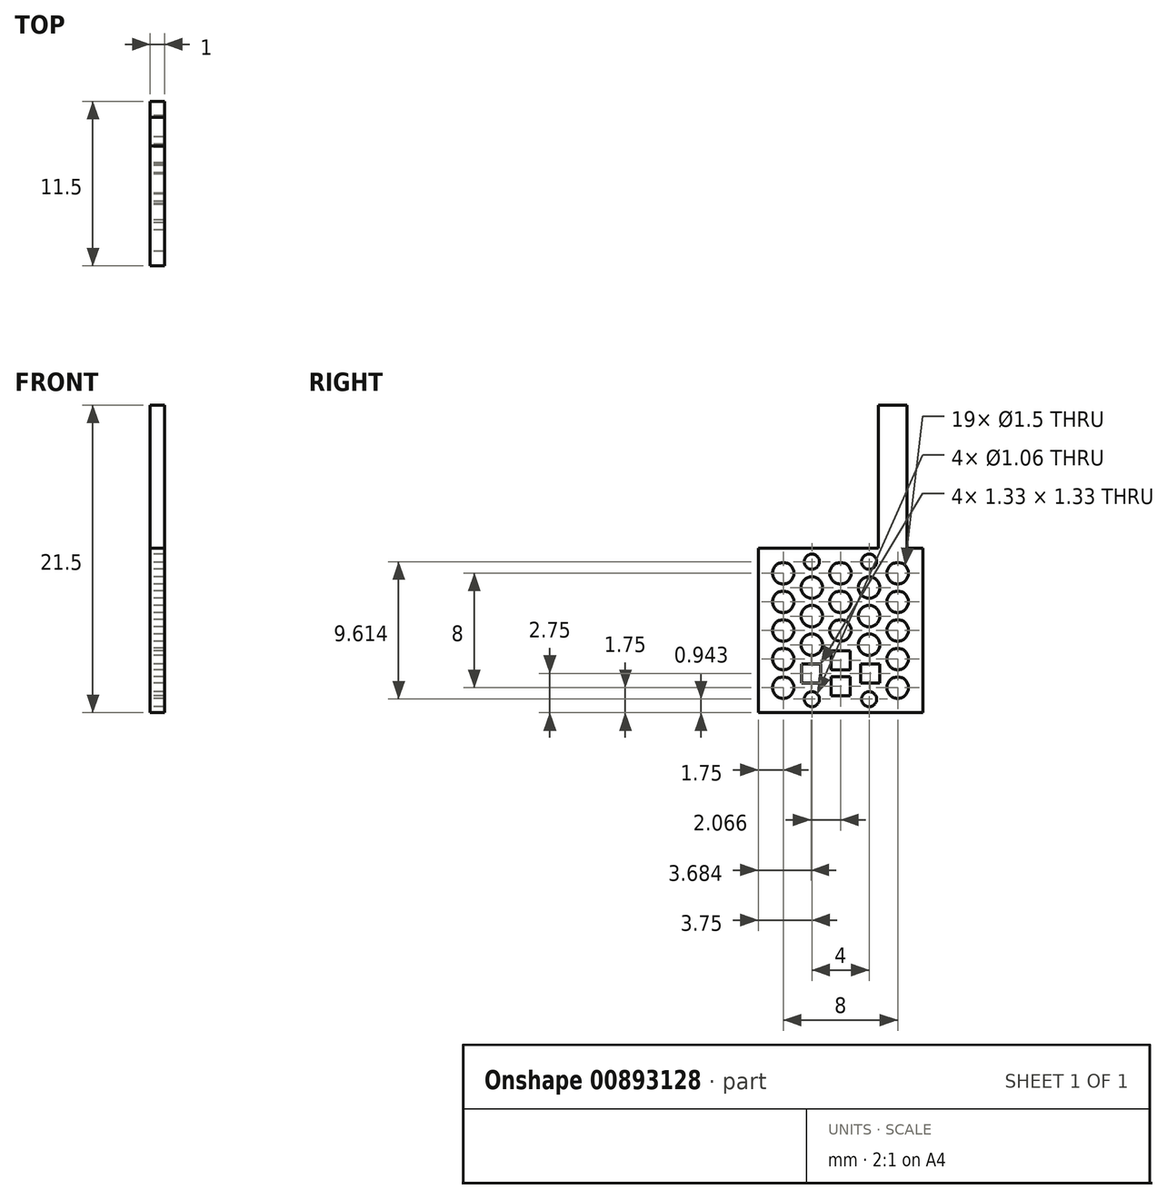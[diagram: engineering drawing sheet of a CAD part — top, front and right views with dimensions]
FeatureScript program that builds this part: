
annotation { "Feature Type Name" : "Feature", "Feature Type Description" : "" }
export const myFeature = defineFeature(function(context is Context, id is Id, definition is map)
    precondition{}
    {
        {
            var Q0;
            Q0=qCreatedBy(makeId("Right.planeOp"),FACE);
            var sketch = newSketch(context, id + "F0", { "sketchPlane" : qUnion([Q0])});
            skLineSegment(sketch, "E0.bottom", {"start": v(0, 0) * mm, "end": v(8.38, 0) * mm});
            skLineSegment(sketch, "E0.top", {"start": v(0, -11.5) * mm, "end": v(11.5, -11.5) * mm});
            skLineSegment(sketch, "E0.left", {"start": v(0, 0) * mm, "end": v(0, -11.5) * mm});
            skLineSegment(sketch, "E1", {"start": v(11.5, 0) * mm, "end": v(11.5, -11.5) * mm});
            skLineSegment(sketch, "E2", {"start": v(10.38, 0) * mm, "end": v(10.38, 10) * mm});
            skLineSegment(sketch, "E3", {"start": v(10.38, 10) * mm, "end": v(8.38, 10) * mm});
            skLineSegment(sketch, "E4", {"start": v(8.38, 10) * mm, "end": v(8.38, 0) * mm});
            skLineSegment(sketch, "E5.trimOffspring", {"start": v(10.38, 0) * mm, "end": v(11.5, 0) * mm});
            skCircle(sketch, "E6", {"center": v(1.75, -5.75) * mm, "radius": 0.75 * mm});
            skCircle(sketch, "E7.MirrorC", {"center": v(1.75, -1.75) * mm, "radius": 0.75 * mm});
            skCircle(sketch, "E8.MirrorC", {"center": v(1.75, -3.75) * mm, "radius": 0.75 * mm});
            skCircle(sketch, "E9.MirrorC", {"center": v(1.75, -9.75) * mm, "radius": 0.75 * mm});
            skCircle(sketch, "E10.MirrorC", {"center": v(1.75, -7.75) * mm, "radius": 0.75 * mm});
            skCircle(sketch, "E11", {"center": v(3.75, -2.75) * mm, "radius": 0.75 * mm});
            skCircle(sketch, "E12", {"center": v(3.75, -10.56) * mm, "radius": 0.53 * mm});
            skCircle(sketch, "E13.MirrorC", {"center": v(5.75, -1.75) * mm, "radius": 0.75 * mm});
            skCircle(sketch, "E14.MirrorC", {"center": v(5.75, -3.75) * mm, "radius": 0.75 * mm});
            skCircle(sketch, "E15.MirrorC", {"center": v(5.75, -5.75) * mm, "radius": 0.75 * mm});
            skCircle(sketch, "E16.MirrorC", {"center": v(7.75, -2.75) * mm, "radius": 0.75 * mm});
            skCircle(sketch, "E17.MirrorC", {"center": v(9.75, -1.75) * mm, "radius": 0.75 * mm});
            skCircle(sketch, "E18.MirrorC", {"center": v(9.75, -3.75) * mm, "radius": 0.75 * mm});
            skCircle(sketch, "E19.MirrorC", {"center": v(9.75, -5.75) * mm, "radius": 0.75 * mm});
            skCircle(sketch, "E20.MirrorC", {"center": v(9.75, -7.75) * mm, "radius": 0.75 * mm});
            skCircle(sketch, "E21.MirrorC", {"center": v(9.75, -9.75) * mm, "radius": 0.75 * mm});
            skCircle(sketch, "E22", {"center": v(7.75, -10.56) * mm, "radius": 0.53 * mm});
            skCircle(sketch, "E23", {"center": v(3.75, -0.94) * mm, "radius": 0.53 * mm});
            skCircle(sketch, "E24", {"center": v(7.75, -0.94) * mm, "radius": 0.53 * mm});
            skCircle(sketch, "E25", {"center": v(3.75, -4.75) * mm, "radius": 0.75 * mm});
            skCircle(sketch, "E26", {"center": v(3.75, -6.75) * mm, "radius": 0.75 * mm});
            skCircle(sketch, "E27.MirrorC", {"center": v(7.75, -4.75) * mm, "radius": 0.75 * mm});
            skCircle(sketch, "E28.MirrorC", {"center": v(7.75, -6.75) * mm, "radius": 0.75 * mm});
            skLineSegment(sketch, "E29", {"start": v(1.75, -1.75) * mm, "end": v(1.75, 0) * mm});
            skLineSegment(sketch, "E30", {"start": v(3.75, -0.94) * mm, "end": v(3.75, 0) * mm});
            skLineSegment(sketch, "E31", {"start": v(5.75, -1.75) * mm, "end": v(5.75, 0) * mm});
            skLineSegment(sketch, "E32", {"start": v(7.75, -0.94) * mm, "end": v(7.75, 0) * mm});
            skLineSegment(sketch, "E33", {"start": v(9.75, -1.75) * mm, "end": v(9.75, 0) * mm});
            skLineSegment(sketch, "E34", {"start": v(5.75, -8.5) * mm, "end": v(6.41, -8.5) * mm});
            skLineSegment(sketch, "E35", {"start": v(6.41, -8.5) * mm, "end": v(6.41, -7.17) * mm});
            skLineSegment(sketch, "E36", {"start": v(6.41, -7.17) * mm, "end": v(6.2, -7.17) * mm});
            skLineSegment(sketch, "E37.MirrorCS", {"start": v(5.75, -9) * mm, "end": v(6.2, -9) * mm});
            skLineSegment(sketch, "E38.MirrorCS", {"start": v(5.75, -9) * mm, "end": v(5.3, -9) * mm});
            skLineSegment(sketch, "E39.MirrorCS", {"start": v(5.75, -8.5) * mm, "end": v(5.09, -8.5) * mm});
            skLineSegment(sketch, "E40.MirrorCS", {"start": v(5.09, -8.5) * mm, "end": v(5.09, -7.17) * mm});
            skLineSegment(sketch, "E41.MirrorCS", {"start": v(5.09, -7.17) * mm, "end": v(6.2, -7.17) * mm});
            skLineSegment(sketch, "E42.MirrorCS", {"start": v(5.75, -9) * mm, "end": v(5.09, -9) * mm});
            skLineSegment(sketch, "E43.MirrorCS", {"start": v(5.09, -9) * mm, "end": v(5.09, -10.33) * mm});
            skLineSegment(sketch, "E44.MirrorCS", {"start": v(5.09, -10.33) * mm, "end": v(6.2, -10.33) * mm});
            skLineSegment(sketch, "E45.MirrorCS", {"start": v(6.41, -9) * mm, "end": v(6.41, -10.33) * mm});
            skLineSegment(sketch, "E46.MirrorCS", {"start": v(5.75, -9) * mm, "end": v(6.41, -9) * mm});
            skLineSegment(sketch, "E47.MirrorCS", {"start": v(6.41, -10.33) * mm, "end": v(6.2, -10.33) * mm});
            skLineSegment(sketch, "E48.0", {"start": v(4.35, -8.09) * mm, "end": v(3.17, -8.09) * mm});
            skLineSegment(sketch, "E49.MirrorCS", {"start": v(4.35, -9.41) * mm, "end": v(3.17, -9.41) * mm});
            skLineSegment(sketch, "E50.0", {"start": v(4.35, -8.75) * mm, "end": v(4.35, -8.09) * mm});
            skLineSegment(sketch, "E51.0", {"start": v(4.35, -8.75) * mm, "end": v(4.35, -9.41) * mm});
            skLineSegment(sketch, "E52.0", {"start": v(3.02, -8.75) * mm, "end": v(3.02, -8.09) * mm});
            skLineSegment(sketch, "E53.0", {"start": v(3.02, -8.75) * mm, "end": v(3.02, -9.41) * mm});
            skLineSegment(sketch, "E54", {"start": v(3.17, -8.09) * mm, "end": v(3.02, -8.09) * mm});
            skLineSegment(sketch, "E55", {"start": v(3.17, -9.41) * mm, "end": v(3.02, -9.41) * mm});
            skPoint(sketch, "E56.end.orphan", {"position": v(5.75, -8.75) * mm});
            skPoint(sketch, "E56.start.orphan", {"position": v(4.5, -8.75) * mm});
            skLineSegment(sketch, "E57.MirrorCS", {"start": v(7.15, -8.09) * mm, "end": v(8.33, -8.09) * mm});
            skLineSegment(sketch, "E58.MirrorCS", {"start": v(8.33, -8.09) * mm, "end": v(8.48, -8.09) * mm});
            skLineSegment(sketch, "E59.MirrorCS", {"start": v(8.48, -8.75) * mm, "end": v(8.48, -8.09) * mm});
            skLineSegment(sketch, "E60.MirrorCS", {"start": v(8.48, -8.75) * mm, "end": v(8.48, -9.41) * mm});
            skLineSegment(sketch, "E61.MirrorCS", {"start": v(7.15, -9.41) * mm, "end": v(8.33, -9.41) * mm});
            skLineSegment(sketch, "E62.MirrorCS", {"start": v(8.33, -9.41) * mm, "end": v(8.48, -9.41) * mm});
            skLineSegment(sketch, "E63.MirrorCS", {"start": v(7.15, -8.75) * mm, "end": v(7.15, -9.41) * mm});
            skLineSegment(sketch, "E64.MirrorCS", {"start": v(7.15, -8.75) * mm, "end": v(7.15, -8.09) * mm});
            skSolve(sketch);
        }
        {
            var Q0;
            Q0=makeQuery(id+"F0.imprint","IMPRINT",FACE,{"disambiguationData":[TD([[makeQuery(id+"F0.imprint","IMPRINT",EDGE,{"derivedFrom":sQuery(id+"F0.wireOp",EDGE,"E0.bottom")}),-1.0]])]});
            var Q1;
            Q1=makeQuery(id+"F0.imprint","IMPRINT",FACE,{"disambiguationData":[TD([[makeQuery(id+"F0.imprint","IMPRINT",EDGE,{"derivedFrom":sQuery(id+"F0.wireOp",EDGE,"r65wuaeR-pUGk-UfhY-v5oq-7bkjaNJfQmKm.bottom")}),-1.0]])]});
            var Q2;
            Q2=makeQuery(id+"F0.imprint","IMPRINT",FACE,{"disambiguationData":[TD([[makeQuery(id+"F0.imprint","IMPRINT",EDGE,{"derivedFrom":sQuery(id+"F0.wireOp",EDGE,"n5EaUuf3-CoM6-EQkv-XzT1-ydr3onYee1LO.bottom")}),1.0]])]});
            var Q3;
            Q3=makeQuery(id+"F0.imprint","IMPRINT",FACE,{"disambiguationData":[TD([[makeQuery(id+"F0.imprint","IMPRINT",EDGE,{"derivedFrom":sQuery(id+"F0.wireOp",EDGE,"2NUbogVr-x7fL-9LVX-WR3f-6RiyyzUn8nbi.bottom")}),-1.0]])]});
            extrude(context, id + "F1", {"entities" : qUnion([Q0, Q1, Q2, Q3]), "depth" : 1 * mm, "offsetDistance" : 25 * mm});
        }
    });
